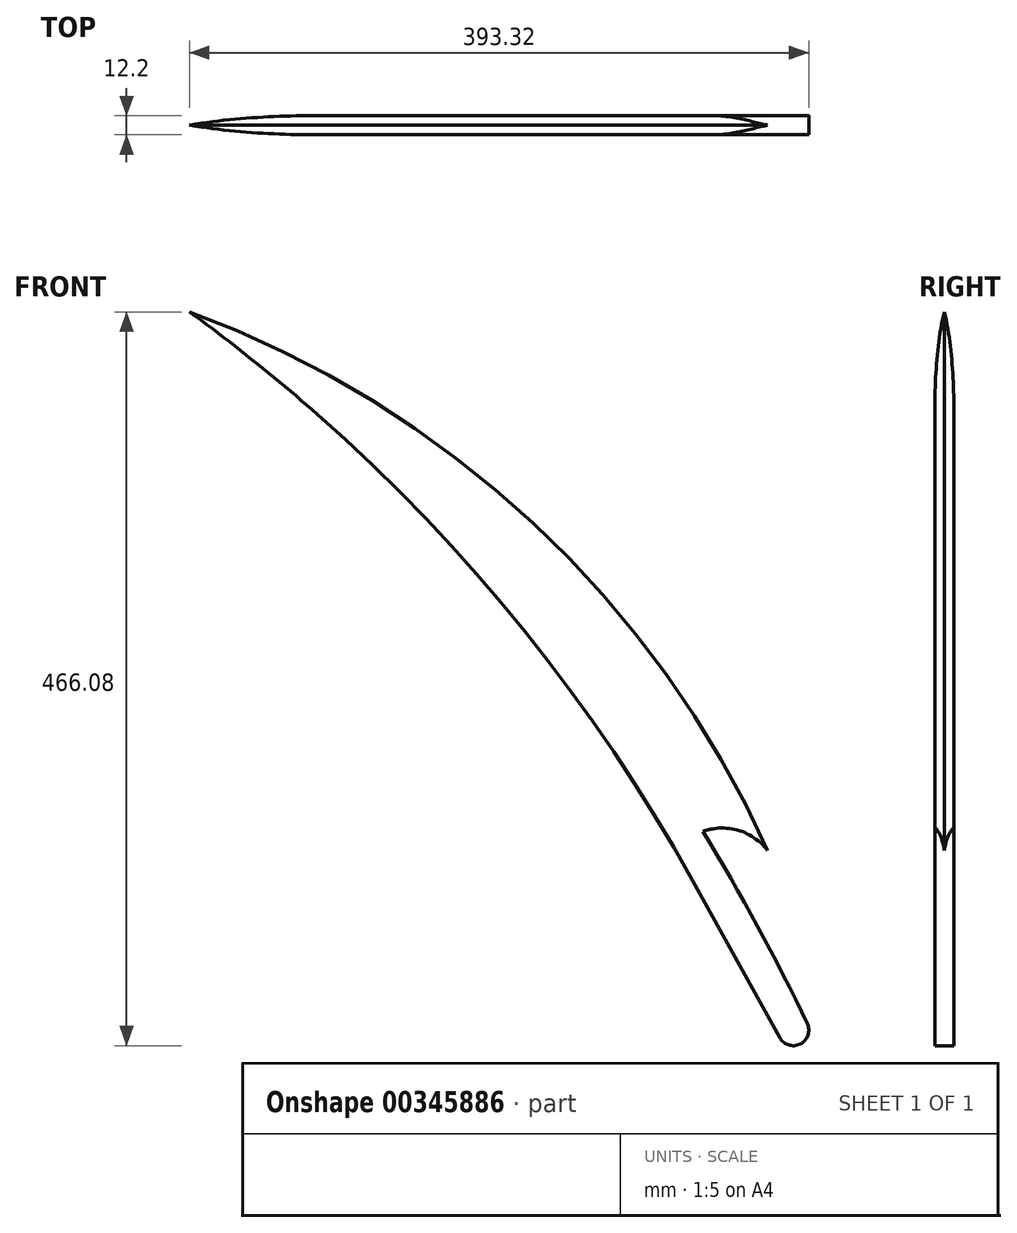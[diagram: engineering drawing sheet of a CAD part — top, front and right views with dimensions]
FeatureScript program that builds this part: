
annotation { "Feature Type Name" : "Feature", "Feature Type Description" : "" }
export const myFeature = defineFeature(function(context is Context, id is Id, definition is map)
    precondition{}
    {
        {
            var Q0;
            Q0=qCreatedBy(makeId("Front.planeOp"),FACE);
            var sketch = newSketch(context, id + "F0", { "sketchPlane" : qUnion([Q0])});
            skArc(sketch, "E0", {"start": v(167.84, -109.93) * mm, "mid": v(18.74, 98.08) * mm, "end": v(-199.27, 232.1) * mm});
            skArc(sketch, "E1", {"start": v(120.14, -128.91) * mm, "mid": v(-19.87, 69.02) * mm, "end": v(-199.27, 232.1) * mm});
            skLineSegment(sketch, "E2", {"start": v(120.14, -128.91) * mm, "end": v(175.69, -228.93) * mm});
            skArc(sketch, "E3", {"start": v(167.84, -109.93) * mm, "mid": v(149.36, -97.22) * mm, "end": v(126.95, -97.8) * mm});
            skArc(sketch, "E4", {"start": v(193.12, -220) * mm, "mid": v(161.53, -158.1) * mm, "end": v(126.95, -97.8) * mm});
            skArc(sketch, "E5", {"start": v(175.69, -228.93) * mm, "mid": v(188.72, -232.9) * mm, "end": v(193.12, -220) * mm});
            skSolve(sketch);
        }
        {
            var Q0;
            Q0=makeQuery(id+"F0.imprint","IMPRINT",FACE,{"disambiguationData":[TD([[makeQuery(id+"F0.imprint","IMPRINT",EDGE,{"derivedFrom":sQuery(id+"F0.wireOp",EDGE,"E0")}),1.0]])]});
            extrude(context, id + "F1", {"entities" : qUnion([Q0]), "depth" : 6.1 * mm});
        }
        {
            var Q0;
            Q0=makeQuery(id+"F1.opExtrude","CAP_EDGE",EDGE,{"disambiguationData":[OSD([sQuery(id+"F0.wireOp",EDGE,"E0")])],"isStart":false});
            fillet(context, id + "F2", {"entities" : qUnion([Q0]), "radius" : 55.19 * mm, "tangentPropagation" : true, "allowEdgeOverflow" : false});
        }
        {
            var Q0;
            Q0=makeQuery(id+"F1.opExtrude","SWEPT_BODY",BODY,{"disambiguationData":[OSD([sQuery(id+"F0.wireOp",EDGE,"E0"),sQuery(id+"F0.wireOp",EDGE,"E1"),sQuery(id+"F0.wireOp",EDGE,"E2"),sQuery(id+"F0.wireOp",EDGE,"E3"),sQuery(id+"F0.wireOp",EDGE,"E4"),sQuery(id+"F0.wireOp",EDGE,"E5")])]});
            var Q1;
            Q1=qCreatedBy(makeId("Front.planeOp"),FACE);
            mirror(context, id + "F3", {"operationType" : NewBodyOperationType.ADD, "entities" : qUnion([Q0]), "mirrorPlane" : qUnion([Q1])});
        }
    });
